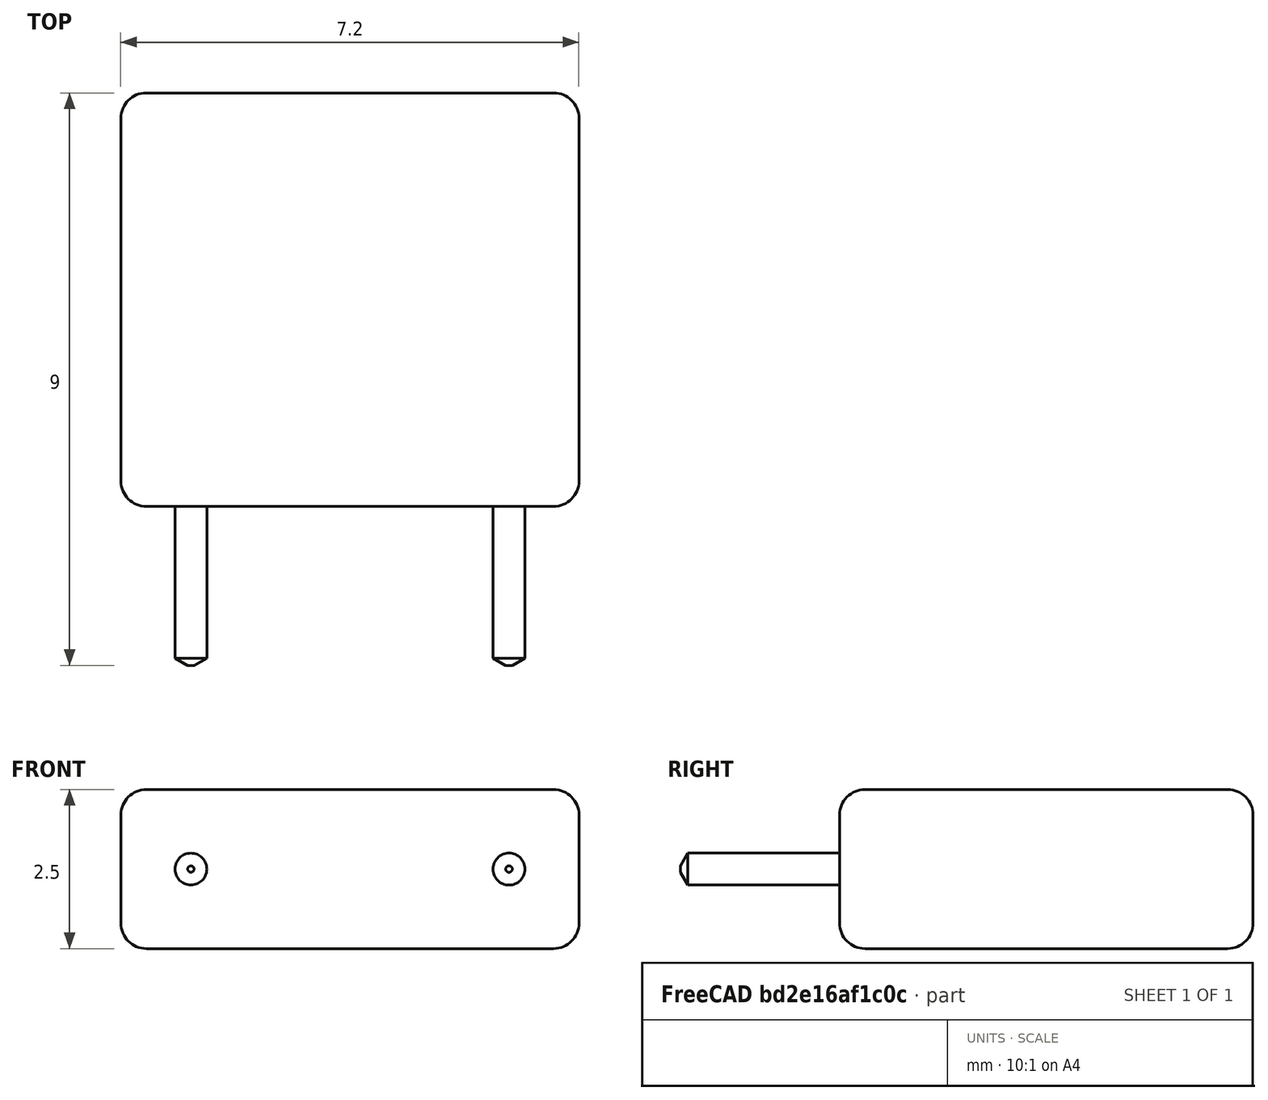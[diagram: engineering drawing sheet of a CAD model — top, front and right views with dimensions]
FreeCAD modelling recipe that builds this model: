
FCSTD DOCUMENT  (FreeCAD 0.17R13528 (Git))
Label: WIMA_A_Case
License: All rights reserved
LicenseURL: http://en.wikipedia.org/wiki/All_rights_reserved
objects: Part::Part2DObjectPython×6, Part::Feature×1
note: 7 computed .brp shape members not serialized (recipe doc carries the construction recipe); baked Part::Feature solids carry a one-line shape summary decoded from their .brp

FEATURE [Part::Part2DObjectPython] ShapeString  label="F_WIMA"  # Draft 2D object (typed FeaturePython)
  FontFile = <userpath>/Desktop/Freecad Projects/calibrib.ttf
  Placement = pos=(-0.75,3.5,1.26) rot=(0,0,1;0rad)
  Size = 1.75
  String = WIMA
  Tracking = 0
FEATURE [Part::Part2DObjectPython] ShapeString001  label="F_Vaule/Rating"  # Draft 2D object (typed FeaturePython)
  FontFile = <userpath>/Desktop/Freecad Projects/calibrib.ttf
  Placement = pos=(-0.65,2.25,1.26) rot=(0,0,1;0rad)
  Size = 1
  String = 4700/400V
  Tracking = 0
FEATURE [Part::Part2DObjectPython] ShapeString002  label="F_Tolerance"  # Draft 2D object (typed FeaturePython)
  FontFile = <userpath>/Desktop/Freecad Projects/calibrib.ttf
  Placement = pos=(-0.65,1,1.26) rot=(0,0,1;0rad)
  Size = 1
  String = 10
  Tracking = 0
FEATURE [Part::Part2DObjectPython] ShapeString003  label="B_WIMA"  # Draft 2D object (typed FeaturePython)
  FontFile = <userpath>/Desktop/Freecad Projects/calibrib.ttf
  Placement = pos=(5,3.5,-1.26) rot=(0,1,0;3.14159rad)
  Size = 1.75
  String = WIMA
  Tracking = 0
FEATURE [Part::Part2DObjectPython] ShapeString004  label="B_Value/Tolerance"  # Draft 2D object (typed FeaturePython)
  FontFile = <userpath>/Desktop/Freecad Projects/calibrib.ttf
  Placement = pos=(4.9,2.25,-1.26) rot=(0,1,0;3.14159rad)
  Size = 1
  String = 4700/400V
  Tracking = 0
FEATURE [Part::Part2DObjectPython] ShapeString005  label="B_Tolerance"  # Draft 2D object (typed FeaturePython)
  FontFile = <userpath>/Desktop/Freecad Projects/calibrib.ttf
  Placement = pos=(4.9,1,-1.26) rot=(0,1,0;3.14159rad)
  Size = 1
  String = 10
  Tracking = 0
FEATURE [Part::Feature] Part__Feature001  label="WIMA_A_Case"
  shape: bbox 7.2 x 9 x 2.5 mm, 36 faces (baked)
